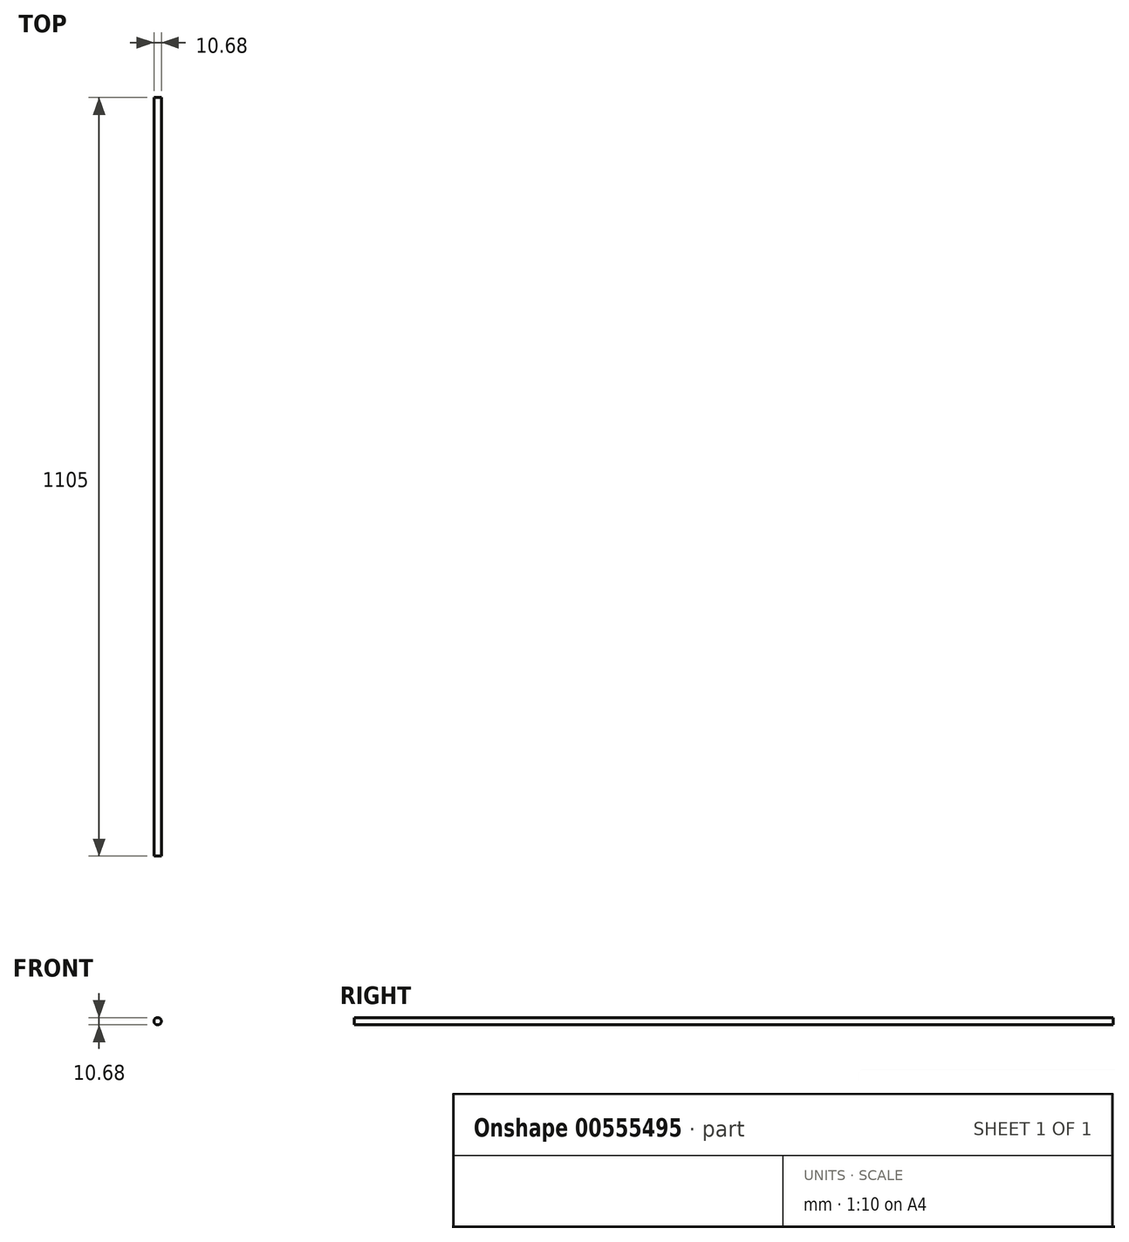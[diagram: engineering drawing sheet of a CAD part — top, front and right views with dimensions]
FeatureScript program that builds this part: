
annotation { "Feature Type Name" : "Feature", "Feature Type Description" : "" }
export const myFeature = defineFeature(function(context is Context, id is Id, definition is map)
    precondition{}
    {
        {
            var Q0;
            Q0=qCreatedBy(makeId("Front.planeOp"),FACE);
            var sketch = newSketch(context, id + "F0", { "sketchPlane" : qUnion([Q0])});
            skCircle(sketch, "E0", {"center": v(0, 0) * mm, "radius": 5.34 * mm});
            skSolve(sketch);
        }
        {
            var Q0;
            Q0 = qSketchRegion(id + "F0", true);
            extrude(context, id + "F1", {"entities" : qUnion([Q0]), "depth" : 1105 * mm, "offsetDistance" : 25 * mm});
        }
    });
